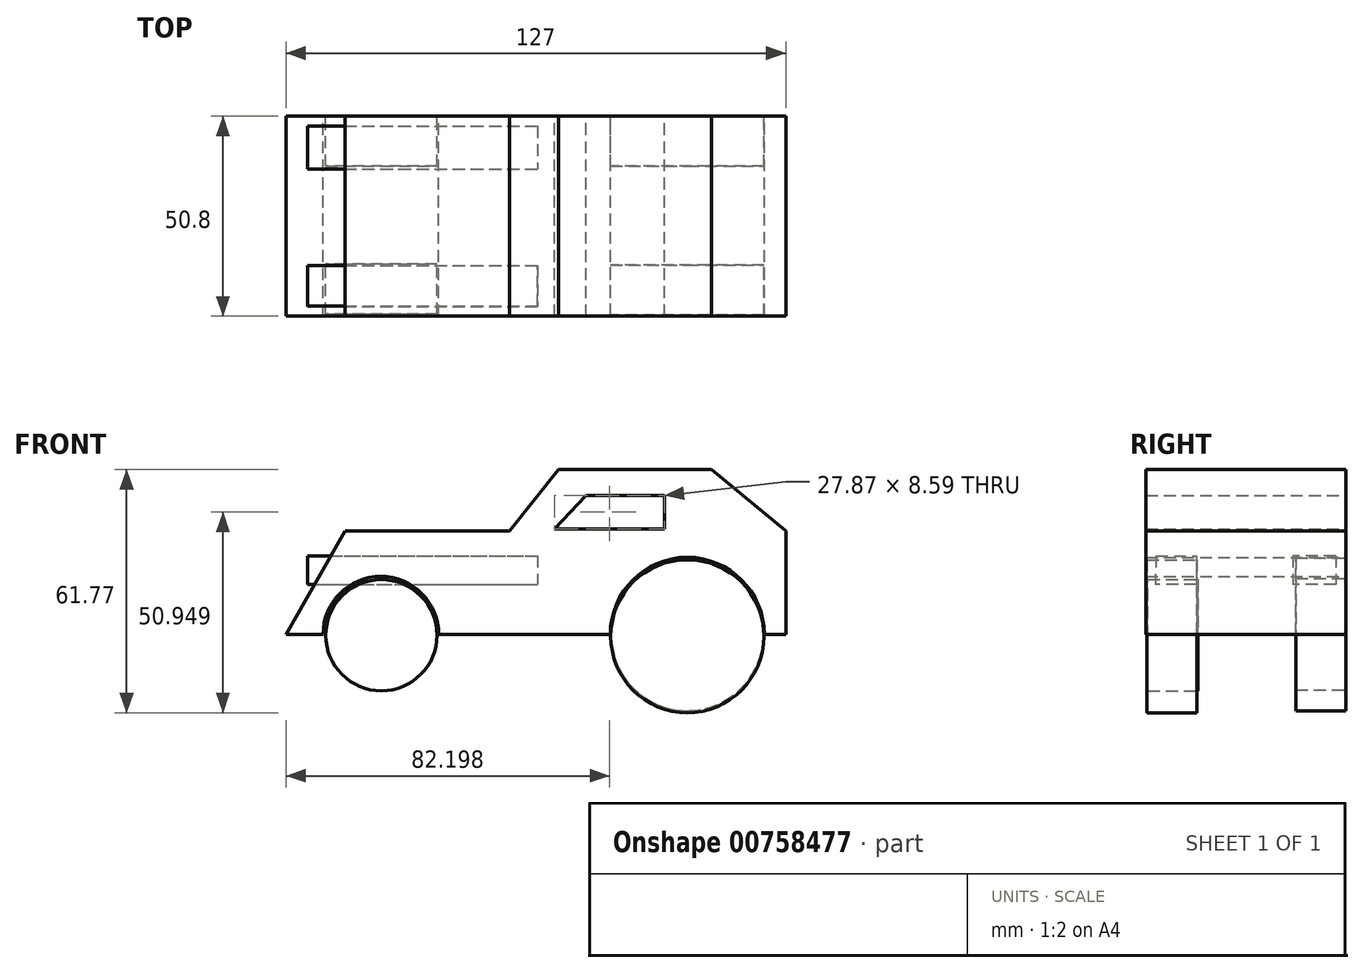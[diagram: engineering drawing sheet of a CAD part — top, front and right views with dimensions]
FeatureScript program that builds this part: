
annotation { "Feature Type Name" : "Feature", "Feature Type Description" : "" }
export const myFeature = defineFeature(function(context is Context, id is Id, definition is map)
    precondition{}
    {
        {
            var Q0;
            Q0=qCreatedBy(makeId("Front.planeOp"),FACE);
            var sketch = newSketch(context, id + "F0", { "sketchPlane" : qUnion([Q0])});
            skSolve(sketch);
        }
        {
            var Q0;
            Q0=qCreatedBy(makeId("Front.planeOp"),FACE);
            var sketch = newSketch(context, id + "F1", { "sketchPlane" : qUnion([Q0])});
            skLineSegment(sketch, "E0", {"start": v(63.04, 0) * mm, "end": v(63.04, 26.25) * mm});
            skLineSegment(sketch, "E1", {"start": v(63.04, 26.25) * mm, "end": v(44.11, 41.82) * mm});
            skLineSegment(sketch, "E2", {"start": v(44.11, 41.82) * mm, "end": v(5.34, 41.82) * mm});
            skLineSegment(sketch, "E3", {"start": v(5.34, 41.82) * mm, "end": v(-7.17, 26.25) * mm});
            skLineSegment(sketch, "E4", {"start": v(-7.17, 26.25) * mm, "end": v(-49, 26.25) * mm});
            skLineSegment(sketch, "E5", {"start": v(-49, 26.25) * mm, "end": v(-63.96, 0) * mm});
            skCircle(sketch, "E6", {"center": v(-39.84, 0) * mm, "radius": 14.69 * mm});
            skCircle(sketch, "E7", {"center": v(38, 0) * mm, "radius": 19.55 * mm});
            skLineSegment(sketch, "E8", {"start": v(-63.96, 0) * mm, "end": v(-54.53, 0) * mm});
            skLineSegment(sketch, "E9", {"start": v(-25.15, 0) * mm, "end": v(18.46, 0) * mm});
            skLineSegment(sketch, "E10", {"start": v(18.46, 0) * mm, "end": v(63.04, 0) * mm});
            skLineSegment(sketch, "E11", {"start": v(57.56, 0) * mm, "end": v(63.04, 0) * mm});
            skLineSegment(sketch, "E12", {"start": v(12.26, 35.3) * mm, "end": v(32.17, 35.3) * mm});
            skLineSegment(sketch, "E13", {"start": v(12.26, 35.3) * mm, "end": v(4.3, 26.7) * mm});
            skLineSegment(sketch, "E14", {"start": v(4.3, 26.7) * mm, "end": v(32.17, 26.7) * mm});
            skLineSegment(sketch, "E15", {"start": v(32.17, 26.7) * mm, "end": v(32.17, 35.3) * mm});
            skSolve(sketch);
        }
        {
            var Q0;
            Q0 = qSketchRegion(id + "F0", true);
            var Q1;
            {var subQ5=sQuery(id+"F1.wireOp",EDGE,"E0");Q1=makeQuery(id+"F1.imprint","IMPRINT",FACE,{"disambiguationData":[TD([[makeQuery(id+"F1.imprint","IMPRINT",EDGE,{"derivedFrom":subQ5}),1.0]])]});}
            var Q2;
            {var subQ0=sQuery(id+"F1.wireOp",EDGE,"E6");var subQ1=sQuery(id+"F1.wireOp",EDGE,"fHXzAilM-Qhat-wzUu-0Ipj-M0EuOXHQcS8Z");var subQ2=makeQuery(id+"F1.imprint","INTERSECT",VERTEX,{"disambiguationData":[OD(0.0)],"derivedFrom":[subQ1,subQ0]});Q2=makeQuery(id+"F1.imprint","IMPRINT",FACE,{"disambiguationData":[TD([[makeQuery(id+"F1.imprint","IMPRINT",EDGE,{"disambiguationData":[TD([[subQ2,-1.0]])],"derivedFrom":subQ1}),1.0]])]});}
            var Q3;
            {var subQ0=sQuery(id+"F1.wireOp",EDGE,"E6");var subQ1=sQuery(id+"F1.wireOp",EDGE,"fHXzAilM-Qhat-wzUu-0Ipj-M0EuOXHQcS8Z");var subQ2=makeQuery(id+"F1.imprint","INTERSECT",VERTEX,{"disambiguationData":[OD(0.0)],"derivedFrom":[subQ1,subQ0]});Q3=makeQuery(id+"F1.imprint","IMPRINT",FACE,{"disambiguationData":[TD([[makeQuery(id+"F1.imprint","IMPRINT",EDGE,{"disambiguationData":[TD([[subQ2,-1.0]])],"derivedFrom":subQ1}),-1.0]])]});}
            var Q4;
            {var subQ0=sQuery(id+"F1.wireOp",EDGE,"E7");var subQ1=sQuery(id+"F1.wireOp",EDGE,"fHXzAilM-Qhat-wzUu-0Ipj-M0EuOXHQcS8Z");var subQ2=makeQuery(id+"F1.imprint","INTERSECT",VERTEX,{"disambiguationData":[OD(0.0)],"derivedFrom":[subQ1,subQ0]});Q4=makeQuery(id+"F1.imprint","IMPRINT",FACE,{"disambiguationData":[TD([[makeQuery(id+"F1.imprint","IMPRINT",EDGE,{"disambiguationData":[TD([[subQ2,-1.0]])],"derivedFrom":subQ1}),1.0]])]});}
            var Q5;
            {var subQ0=sQuery(id+"F1.wireOp",EDGE,"E7");var subQ1=sQuery(id+"F1.wireOp",EDGE,"fHXzAilM-Qhat-wzUu-0Ipj-M0EuOXHQcS8Z");var subQ2=makeQuery(id+"F1.imprint","INTERSECT",VERTEX,{"disambiguationData":[OD(0.0)],"derivedFrom":[subQ1,subQ0]});Q5=makeQuery(id+"F1.imprint","IMPRINT",FACE,{"disambiguationData":[TD([[makeQuery(id+"F1.imprint","IMPRINT",EDGE,{"disambiguationData":[TD([[subQ2,-1.0]])],"derivedFrom":subQ1}),-1.0]])]});}
            extrude(context, id + "F2", {"entities" : qUnion([Q0, Q1, Q2, Q3, Q4, Q5]), "depth" : 50.8 * mm, "offsetDistance" : 25.4 * mm});
        }
        {
            var Q0;
            Q0=qCreatedBy(makeId("Front.planeOp"),FACE);
            var sketch = newSketch(context, id + "F3", { "sketchPlane" : qUnion([Q0])});
            skCircle(sketch, "E16", {"center": v(-39.7, 0) * mm, "radius": 14.13 * mm});
            skCircle(sketch, "E17", {"center": v(38, 0) * mm, "radius": 19.44 * mm});
            skSolve(sketch);
        }
        {
            var Q0;
            Q0 = qSketchRegion(id + "F3", true);
            extrude(context, id + "F4", {"entities" : qUnion([Q0]), "depth" : 12.7 * mm, "offsetDistance" : 25.4 * mm});
        }
        {
            var Q0;
            Q0=makeQuery(id+"F4.opExtrude","SWEPT_BODY",BODY,{"disambiguationData":[OSD([sQuery(id+"F3.wireOp",EDGE,"E16")])]});
            transform(context, id + "F5", {"entities" : qUnion([Q0]), "transformType" : TransformType.TRANSLATION_3D, "dx" : 0 * mm, "dy" : 0 * mm, "dz" : 0 * mm, "makeCopy" : true});
        }
        {
            var Q0;
            Q0=makeQuery(id+"F5.opPattern","COPY",BODY,{"derivedFrom":makeQuery(id+"F4.opExtrude","SWEPT_BODY",BODY,{"disambiguationData":[OSD([sQuery(id+"F3.wireOp",EDGE,"E16")])]}),"instanceName":"1"});
            deleteBodies(context, id + "F6", {"entities" : qUnion([Q0])});
        }
        {
            var Q0;
            Q0=makeQuery(id+"F4.opExtrude","SWEPT_BODY",BODY,{"disambiguationData":[OSD([sQuery(id+"F3.wireOp",EDGE,"E17")])]});
            transform(context, id + "F7", {"entities" : qUnion([Q0]), "transformType" : TransformType.TRANSLATION_3D, "dx" : 0 * mm, "dy" : -37.85 * mm, "dz" : -0.5 * mm, "makeCopy" : true});
        }
        {
            var Q0;
            Q0=makeQuery(id+"F4.opExtrude","SWEPT_BODY",BODY,{"disambiguationData":[OSD([sQuery(id+"F3.wireOp",EDGE,"E16")])]});
            transform(context, id + "F8", {"entities" : qUnion([Q0]), "transformType" : TransformType.TRANSLATION_3D, "dx" : 0 * mm, "dy" : -37.6 * mm, "dz" : -0.25 * mm, "makeCopy" : true});
        }
        {
            var Q0;
            Q0=qCreatedBy(makeId("Right.planeOp"),FACE);
            var sketch = newSketch(context, id + "F9", { "sketchPlane" : qUnion([Q0])});
            skLineSegment(sketch, "E18", {"start": v(-2.55, 19.91) * mm, "end": v(-13.48, 19.91) * mm});
            skLineSegment(sketch, "E19", {"start": v(-2.55, 19.91) * mm, "end": v(-2.55, 12.63) * mm});
            skLineSegment(sketch, "E20", {"start": v(-13.48, 19.91) * mm, "end": v(-13.48, 12.63) * mm});
            skLineSegment(sketch, "E21", {"start": v(-2.55, 12.63) * mm, "end": v(-13.48, 12.63) * mm});
            skLineSegment(sketch, "E22", {"start": v(-48.2, 19.91) * mm, "end": v(-38, 19.91) * mm});
            skLineSegment(sketch, "E23", {"start": v(-38, 19.91) * mm, "end": v(-38, 12.63) * mm});
            skLineSegment(sketch, "E24", {"start": v(-38, 12.63) * mm, "end": v(-48.4, 12.63) * mm});
            skLineSegment(sketch, "E25", {"start": v(-48.2, 19.91) * mm, "end": v(-48.4, 12.63) * mm});
            skSolve(sketch);
        }
        {
            var Q0;
            Q0 = qSketchRegion(id + "F9", true);
            extrude(context, id + "F10", {"entities" : qUnion([Q0]), "oppositeDirection" : true, "depth" : 58.42 * mm, "offsetDistance" : 25.4 * mm});
        }
    });
